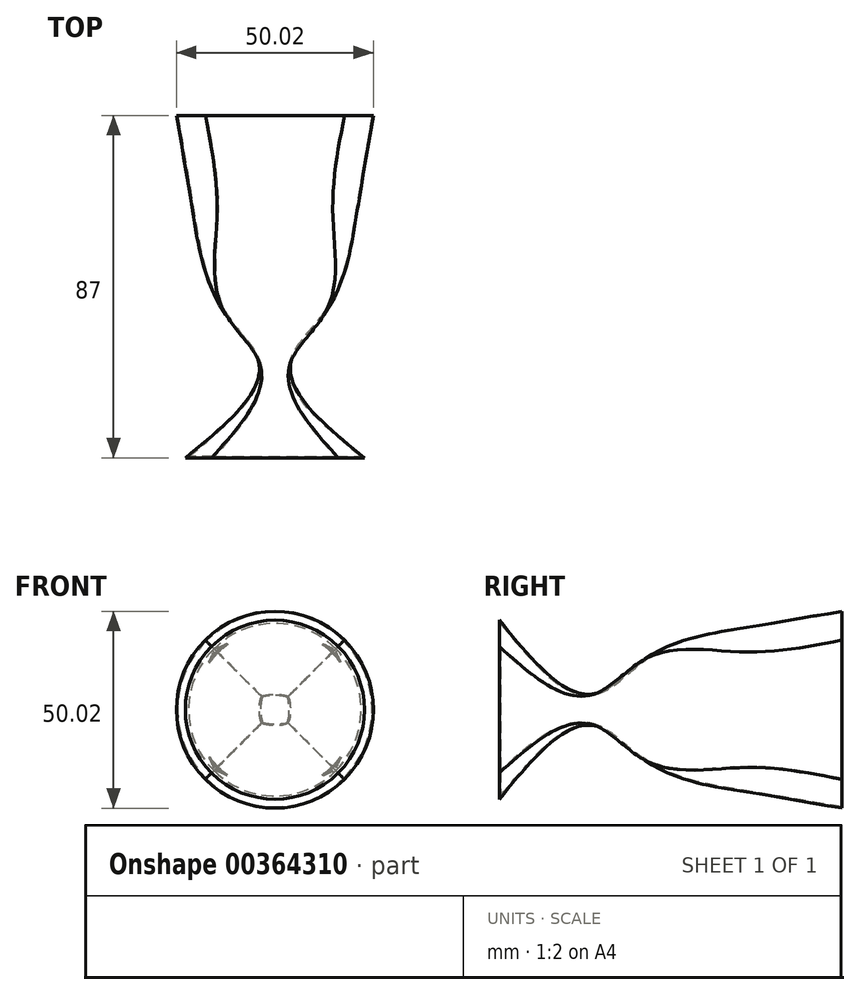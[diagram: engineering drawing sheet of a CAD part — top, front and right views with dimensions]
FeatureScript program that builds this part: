
annotation { "Feature Type Name" : "Feature", "Feature Type Description" : "" }
export const myFeature = defineFeature(function(context is Context, id is Id, definition is map)
    precondition{}
    {
        {
            var Q0;
            Q0=qCreatedBy(makeId("Front.planeOp"),FACE);
            var sketch = newSketch(context, id + "F0", { "sketchPlane" : qUnion([Q0])});
            skCircle(sketch, "E0", {"center": v(0, 0) * mm, "radius": 25 * mm});
            skSolve(sketch);
        }
        {
            var Q0;
            Q0=qCreatedBy(makeId("Front.planeOp"),FACE);
            cPlane(context, id + "F1", {"entities" : qUnion([Q0]), "cplaneType" : CPlaneType.OFFSET, "offset" : 25 * mm, "width" : 150 * mm, "height" : 150 * mm});
        }
        {
            var Q0;
            Q0=qCreatedBy(id+"F1.planeOp",FACE);
            var sketch = newSketch(context, id + "F2", { "sketchPlane" : qUnion([Q0])});
            skCircle(sketch, "E1", {"center": v(0, 0) * mm, "radius": 20.78 * mm});
            skSolve(sketch);
        }
        {
            var Q0;
            Q0=qCreatedBy(id+"F1.planeOp",FACE);
            cPlane(context, id + "F3", {"entities" : qUnion([Q0]), "cplaneType" : CPlaneType.OFFSET, "offset" : 25 * mm, "width" : 150 * mm, "height" : 150 * mm});
        }
        {
            var Q0;
            Q0=qCreatedBy(id+"F3.planeOp",FACE);
            var sketch = newSketch(context, id + "F4", { "sketchPlane" : qUnion([Q0])});
            skLineSegment(sketch, "E2.bottom", {"start": v(12.86, -12.86) * mm, "end": v(-12.86, -12.86) * mm});
            skLineSegment(sketch, "E2.top", {"start": v(12.86, 12.86) * mm, "end": v(-12.86, 12.86) * mm});
            skLineSegment(sketch, "E2.left", {"start": v(12.86, -12.86) * mm, "end": v(12.86, 12.86) * mm});
            skLineSegment(sketch, "E2.right", {"start": v(-12.86, -12.86) * mm, "end": v(-12.86, 12.86) * mm});
            skPoint(sketch, "E2.middle", {"position": v(0, 0) * mm});
            skSolve(sketch);
        }
        {
            var Q0;
            Q0=qCreatedBy(id+"F3.planeOp",FACE);
            cPlane(context, id + "F5", {"entities" : qUnion([Q0]), "cplaneType" : CPlaneType.OFFSET, "offset" : 12 * mm, "width" : 150 * mm, "height" : 150 * mm});
        }
        {
            var Q0;
            Q0=qCreatedBy(id+"F5.planeOp",FACE);
            var sketch = newSketch(context, id + "F6", { "sketchPlane" : qUnion([Q0])});
            skLineSegment(sketch, "E3.bottom", {"start": v(4.29, -4.29) * mm, "end": v(-4.29, -4.29) * mm});
            skLineSegment(sketch, "E3.top", {"start": v(4.29, 4.29) * mm, "end": v(-4.29, 4.29) * mm});
            skLineSegment(sketch, "E3.left", {"start": v(4.29, -4.29) * mm, "end": v(4.29, 4.29) * mm});
            skLineSegment(sketch, "E3.right", {"start": v(-4.29, -4.29) * mm, "end": v(-4.29, 4.29) * mm});
            skPoint(sketch, "E3.middle", {"position": v(0, 0) * mm});
            skSolve(sketch);
        }
        {
            var Q0;
            Q0=qCreatedBy(id+"F5.planeOp",FACE);
            cPlane(context, id + "F7", {"entities" : qUnion([Q0]), "cplaneType" : CPlaneType.OFFSET, "offset" : 25 * mm, "width" : 150 * mm, "height" : 150 * mm});
        }
        {
            var Q0;
            Q0=qCreatedBy(id+"F7.planeOp",FACE);
            var sketch = newSketch(context, id + "F8", { "sketchPlane" : qUnion([Q0])});
            skCircle(sketch, "E4", {"center": v(0, 0) * mm, "radius": 22.75 * mm});
            skSolve(sketch);
        }
        {
            var Q0;
            Q0=makeQuery(id+"F0.imprint","IMPRINT",FACE,{"disambiguationData":[TD([[makeQuery(id+"F0.imprint","IMPRINT",EDGE,{"derivedFrom":sQuery(id+"F0.wireOp",EDGE,"E0")}),1.0]])]});
            var Q1;
            Q1=makeQuery(id+"F2.imprint","IMPRINT",FACE,{"disambiguationData":[TD([[makeQuery(id+"F2.imprint","IMPRINT",EDGE,{"derivedFrom":sQuery(id+"F2.wireOp",EDGE,"E1")}),1.0]])]});
            var Q2;
            Q2=makeQuery(id+"F4.imprint","IMPRINT",FACE,{"disambiguationData":[TD([[makeQuery(id+"F4.imprint","IMPRINT",EDGE,{"derivedFrom":sQuery(id+"F4.wireOp",EDGE,"E2.bottom")}),-1.0]])]});
            var Q3;
            Q3=makeQuery(id+"F6.imprint","IMPRINT",FACE,{"disambiguationData":[TD([[makeQuery(id+"F6.imprint","IMPRINT",EDGE,{"derivedFrom":sQuery(id+"F6.wireOp",EDGE,"E3.bottom")}),-1.0]])]});
            var Q4;
            Q4=makeQuery(id+"F8.imprint","IMPRINT",FACE,{"disambiguationData":[TD([[makeQuery(id+"F8.imprint","IMPRINT",EDGE,{"derivedFrom":sQuery(id+"F8.wireOp",EDGE,"E4")}),1.0]])]});
            loft(context, id + "F9", {"sheetProfilesArray" : [{ "sheetProfileEntities" : qUnion([Q0]) }, { "sheetProfileEntities" : qUnion([Q1]) }, { "sheetProfileEntities" : qUnion([Q2]) }, { "sheetProfileEntities" : qUnion([Q3]) }, { "sheetProfileEntities" : qUnion([Q4]) }]});
        }
        {
            var Q0;
            Q0=makeQuery(id+"F9.opLoft","CAP_FACE",FACE,{"disambiguationData":[OSD([makeQuery(id+"F0.imprint","IMPRINT",FACE,{"disambiguationData":[TD([[makeQuery(id+"F0.imprint","IMPRINT",EDGE,{"derivedFrom":sQuery(id+"F0.wireOp",EDGE,"E0")}),1.0]])]})])],"isStart":true});
            shell(context, id + "F10", {"entities" : qUnion([Q0]), "thickness" : .3 * mm});
        }
    });
